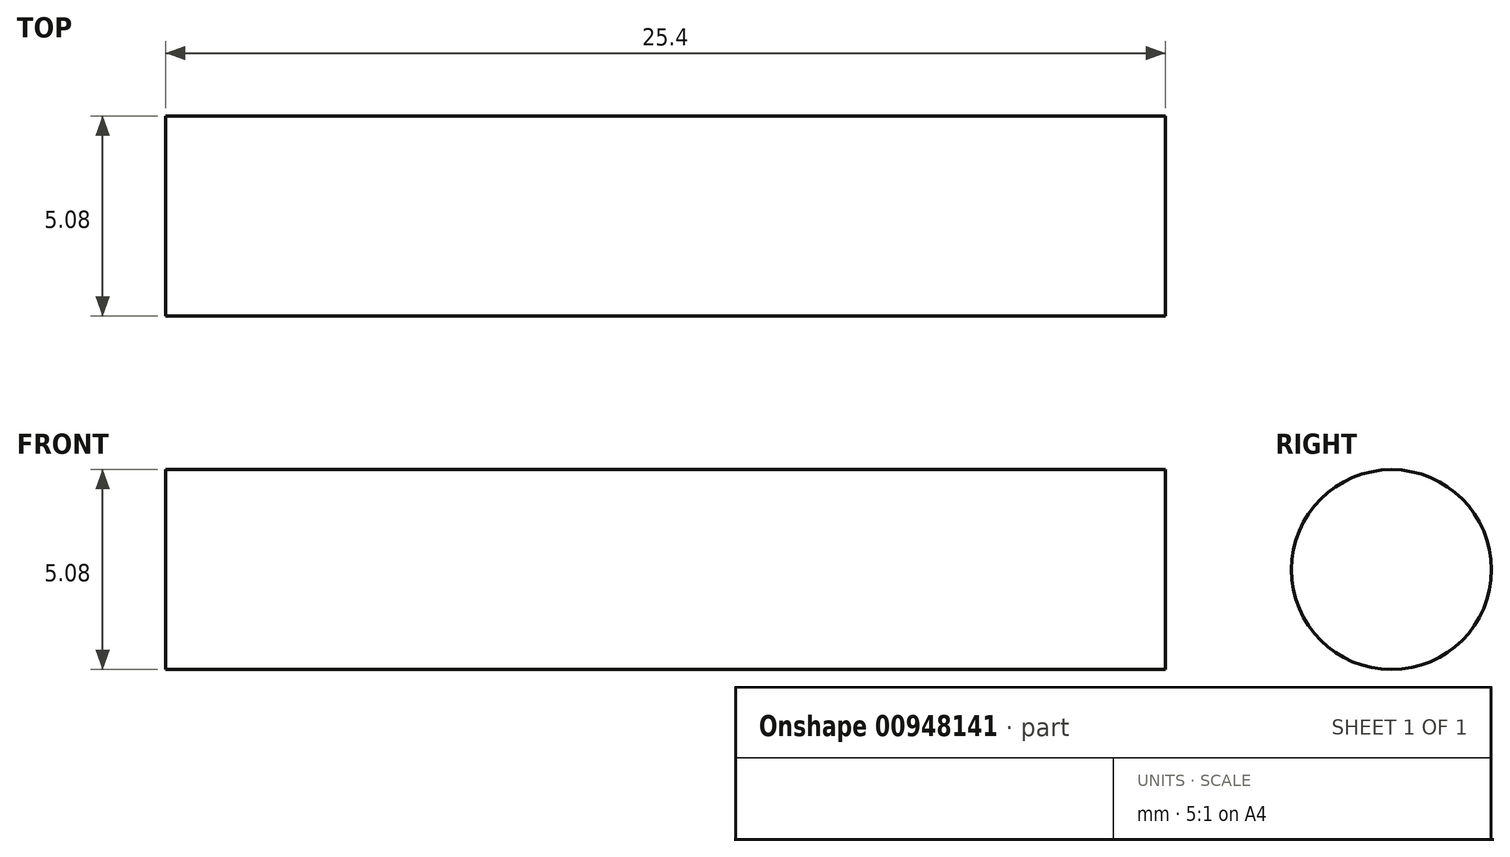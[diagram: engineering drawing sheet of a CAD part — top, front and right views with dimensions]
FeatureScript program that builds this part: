
annotation { "Feature Type Name" : "Feature", "Feature Type Description" : "" }
export const myFeature = defineFeature(function(context is Context, id is Id, definition is map)
    precondition{}
    {
        {
            var Q0;
            Q0=qCreatedBy(makeId("Right.planeOp"),FACE);
            var sketch = newSketch(context, id + "F0", { "sketchPlane" : qUnion([Q0])});
            skCircle(sketch, "E0", {"center": v(-57.84, 27.72) * mm, "radius": 2.54 * mm});
            skSolve(sketch);
        }
        {
            var Q0;
            Q0=makeQuery(id+"F0.imprint","IMPRINT",FACE,{"disambiguationData":[TD([[makeQuery(id+"F0.imprint","IMPRINT",EDGE,{"derivedFrom":sQuery(id+"F0.wireOp",EDGE,"E0")}),1.0]])]});
            extrude(context, id + "F1", {"entities" : qUnion([Q0]), "depth" : 25.4 * mm, "offsetDistance" : 25.4 * mm});
        }
    });
